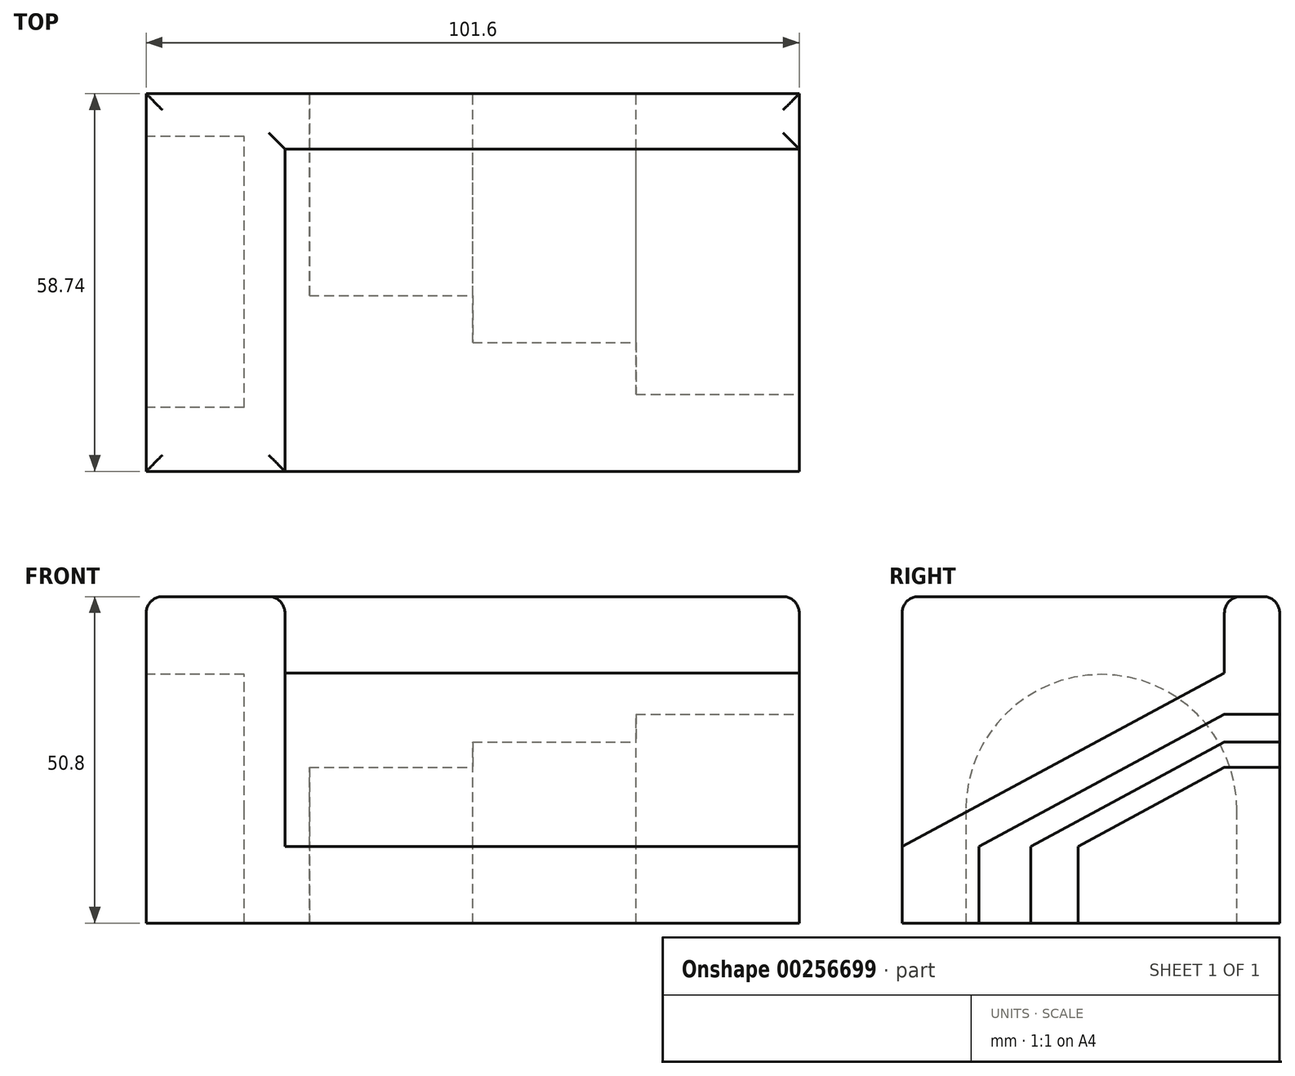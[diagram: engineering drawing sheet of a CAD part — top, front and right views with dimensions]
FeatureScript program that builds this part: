
annotation { "Feature Type Name" : "Feature", "Feature Type Description" : "" }
export const myFeature = defineFeature(function(context is Context, id is Id, definition is map)
    precondition{}
    {
        {
            var Q0;
            Q0=qCreatedBy(makeId("Top.planeOp"),FACE);
            var sketch = newSketch(context, id + "F0", { "sketchPlane" : qUnion([Q0])});
            skLineSegment(sketch, "E0.bottom", {"start": v(38.1, 29.37) * mm, "end": v(-38.1, 29.37) * mm});
            skLineSegment(sketch, "E0.top", {"start": v(38.1, -29.37) * mm, "end": v(-38.1, -29.37) * mm});
            skLineSegment(sketch, "E0.left", {"start": v(38.1, 29.37) * mm, "end": v(38.1, -29.37) * mm});
            skLineSegment(sketch, "E0.right", {"start": v(-38.1, 29.37) * mm, "end": v(-38.1, -29.37) * mm});
            skPoint(sketch, "E0.middle", {"position": v(0, 0) * mm});
            skLineSegment(sketch, "E1.bottom", {"start": v(-38.1, -29.37) * mm, "end": v(-50.8, -29.37) * mm});
            skLineSegment(sketch, "E1.top", {"start": v(-38.1, 29.37) * mm, "end": v(-50.8, 29.37) * mm});
            skLineSegment(sketch, "E1.left", {"start": v(-38.1, -29.37) * mm, "end": v(-38.1, 29.37) * mm});
            skLineSegment(sketch, "E1.right", {"start": v(-50.8, -29.37) * mm, "end": v(-50.8, 29.37) * mm});
            skLineSegment(sketch, "E2.bottom", {"start": v(38.1, 29.37) * mm, "end": v(50.8, 29.37) * mm});
            skLineSegment(sketch, "E2.top", {"start": v(38.1, -29.37) * mm, "end": v(50.8, -29.37) * mm});
            skLineSegment(sketch, "E2.right", {"start": v(50.8, 29.37) * mm, "end": v(50.8, -29.37) * mm});
            skSolve(sketch);
        }
        {
            var Q0;
            Q0 = qSketchRegion(id + "F0", true);
            extrude(context, id + "F1", {"entities" : qUnion([Q0]), "depth" : 50.8 * mm});
        }
        {
            var Q0;
            Q0=makeQuery(id+"F1.opExtrude","SWEPT_FACE",FACE,{"disambiguationData":[OSD([sQuery(id+"F0.wireOp",EDGE,"E1.right")])]});
            var sketch = newSketch(context, id + "F2", { "sketchPlane" : qUnion([Q0])});
            skLineSegment(sketch, "E3", {"start": v(-22.71, 0) * mm, "end": v(-22.71, 17.6) * mm});
            skLineSegment(sketch, "E4", {"start": v(19.45, 17.6) * mm, "end": v(19.45, 0) * mm});
            skArc(sketch, "E5", {"start": v(19.45, 17.6) * mm, "mid": v(-1.63, 38.68) * mm, "end": v(-22.71, 17.6) * mm});
            skSolve(sketch);
        }
        {
            var Q0;
            {var subQ0=sQuery(id+"F2.wireOp",EDGE,"E3");Q0=makeQuery(id+"F2.imprint","IMPRINT",FACE,{"disambiguationData":[TD([[makeQuery(id+"F2.imprint","IMPRINT",EDGE,{"derivedFrom":subQ0}),-1.0]])]});}
            extrude(context, id + "F3", {"entities" : qUnion([Q0]), "operationType" : NewBodyOperationType.REMOVE, "oppositeDirection" : true, "depth" : 15.24 * mm});
        }
        {
            var Q0;
            Q0=makeQuery(id+"F1.opExtrude","SWEPT_FACE",FACE,{"disambiguationData":[OSD([sQuery(id+"F0.wireOp",EDGE,"E2.right")])]});
            var sketch = newSketch(context, id + "F4", { "sketchPlane" : qUnion([Q0])});
            skLineSegment(sketch, "E6", {"start": v(-29.37, 11.94) * mm, "end": v(20.78, 38.92) * mm});
            skLineSegment(sketch, "E7", {"start": v(20.78, 38.92) * mm, "end": v(20.78, 50.8) * mm});
            skLineSegment(sketch, "E8", {"start": v(20.78, 50.8) * mm, "end": v(-29.37, 50.8) * mm});
            skLineSegment(sketch, "E9", {"start": v(-29.37, 50.8) * mm, "end": v(-29.37, 11.94) * mm});
            skSolve(sketch);
        }
        {
            var Q0;
            Q0 = qSketchRegion(id + "F4", true);
            extrude(context, id + "F5", {"entities" : qUnion([Q0]), "operationType" : NewBodyOperationType.REMOVE, "oppositeDirection" : true, "depth" : 80 * mm});
        }
        {
            var Q0;
            Q0=makeQuery(id+"F1.opExtrude","SWEPT_FACE",FACE,{"disambiguationData":[OSD([sQuery(id+"F0.wireOp",EDGE,"E2.right")])]});
            var sketch = newSketch(context, id + "F6", { "sketchPlane" : qUnion([Q0])});
            skLineSegment(sketch, "E10", {"start": v(-17.42, 0) * mm, "end": v(-17.42, 11.94) * mm});
            skLineSegment(sketch, "E11", {"start": v(-17.42, 11.94) * mm, "end": v(20.78, 32.49) * mm});
            skLineSegment(sketch, "E12", {"start": v(20.78, 0) * mm, "end": v(-17.42, 0) * mm});
            skLineSegment(sketch, "E13", {"start": v(20.78, 32.49) * mm, "end": v(29.37, 32.49) * mm});
            skLineSegment(sketch, "E14", {"start": v(29.37, 32.49) * mm, "end": v(29.37, 0) * mm});
            skLineSegment(sketch, "E15", {"start": v(29.37, 0) * mm, "end": v(20.78, 0) * mm});
            skSolve(sketch);
        }
        {
            var Q0;
            Q0 = qSketchRegion(id + "F6", true);
            extrude(context, id + "F7", {"entities" : qUnion([Q0]), "operationType" : NewBodyOperationType.REMOVE, "oppositeDirection" : true, "depth" : 25.4 * mm});
        }
        {
            var Q0;
            Q0=makeQuery(id+"F1.opExtrude","CAP_FACE",FACE,{"disambiguationData":[OSD([sQuery(id+"F0.wireOp",EDGE,"E0.bottom"),sQuery(id+"F0.wireOp",EDGE,"E0.top"),sQuery(id+"F0.wireOp",EDGE,"E1.bottom"),sQuery(id+"F0.wireOp",EDGE,"E1.top"),sQuery(id+"F0.wireOp",EDGE,"E1.right"),sQuery(id+"F0.wireOp",EDGE,"E2.bottom"),sQuery(id+"F0.wireOp",EDGE,"E2.top"),sQuery(id+"F0.wireOp",EDGE,"E2.right")])],"isStart":false});
            var Q1;
            Q1=makeQuery(id+"F3.boolean.opBoolean","COPY",EDGE,{"derivedFrom":makeQuery(id+"F3.opExtrude","CAP_EDGE",EDGE,{"disambiguationData":[OSD([sQuery(id+"F2.wireOp",EDGE,"E5")])],"isStart":true})});
            fillet(context, id + "F8", {"entities" : qUnion([Q0, Q1]), "radius" : 2.54 * mm, "tangentPropagation" : true, "allowEdgeOverflow" : false});
        }
        {
            var Q0;
            Q0=makeQuery(id+"F7.boolean.opBoolean","COPY",FACE,{"derivedFrom":makeQuery(id+"F7.opExtrude","CAP_FACE",FACE,{"disambiguationData":[OSD([sQuery(id+"F6.wireOp",EDGE,"E10"),sQuery(id+"F6.wireOp",EDGE,"E11"),sQuery(id+"F6.wireOp",EDGE,"E12"),sQuery(id+"F6.wireOp",EDGE,"E13"),sQuery(id+"F6.wireOp",EDGE,"E14"),sQuery(id+"F6.wireOp",EDGE,"E15")])],"isStart":false})});
            var sketch = newSketch(context, id + "F9", { "sketchPlane" : qUnion([Q0])});
            skLineSegment(sketch, "E16", {"start": v(-9.33, 0) * mm, "end": v(-9.33, 11.94) * mm});
            skLineSegment(sketch, "E17", {"start": v(-9.33, 11.94) * mm, "end": v(20.78, 28.14) * mm});
            skLineSegment(sketch, "E18", {"start": v(20.78, 28.14) * mm, "end": v(29.37, 28.14) * mm});
            skLineSegment(sketch, "E19", {"start": v(29.37, 28.14) * mm, "end": v(29.37, 0) * mm});
            skLineSegment(sketch, "E20", {"start": v(29.37, 0) * mm, "end": v(-9.33, 0) * mm});
            skSolve(sketch);
        }
        {
            var Q0;
            Q0 = qSketchRegion(id + "F9", true);
            extrude(context, id + "F10", {"entities" : qUnion([Q0]), "operationType" : NewBodyOperationType.REMOVE, "oppositeDirection" : true, "depth" : 25.4 * mm});
        }
        {
            var Q0;
            Q0=qCreatedBy(makeId("Top.planeOp"),FACE);
            var sketch = newSketch(context, id + "F11", { "sketchPlane" : qUnion([Q0])});
            skLineSegment(sketch, "E21.bottom", {"start": v(67.07, 3) * mm, "end": v(23.4, 3) * mm});
            skLineSegment(sketch, "E21.top", {"start": v(67.07, 30.2) * mm, "end": v(23.4, 30.2) * mm});
            skLineSegment(sketch, "E21.left", {"start": v(67.07, 3) * mm, "end": v(67.07, 30.2) * mm});
            skLineSegment(sketch, "E21.right", {"start": v(23.4, 3) * mm, "end": v(23.4, 30.2) * mm});
            skSolve(sketch);
        }
        {
            var Q0;
            Q0 = qSketchRegion(id + "F11", true);
            extrude(context, id + "F12", {"entities" : qUnion([Q0]), "operationType" : NewBodyOperationType.REMOVE, "oppositeDirection" : true, "depth" : 25.4 * mm});
        }
        {
            var Q0;
            Q0=makeQuery(id+"F10.boolean.opBoolean","COPY",FACE,{"derivedFrom":makeQuery(id+"F10.opExtrude","CAP_FACE",FACE,{"disambiguationData":[OSD([sQuery(id+"F9.wireOp",EDGE,"E16"),sQuery(id+"F9.wireOp",EDGE,"E17"),sQuery(id+"F9.wireOp",EDGE,"E18"),sQuery(id+"F9.wireOp",EDGE,"E19"),sQuery(id+"F9.wireOp",EDGE,"E20")])],"isStart":false})});
            var sketch = newSketch(context, id + "F13", { "sketchPlane" : qUnion([Q0])});
            skLineSegment(sketch, "E22", {"start": v(-2.01, 0) * mm, "end": v(-2.01, 11.94) * mm});
            skLineSegment(sketch, "E23", {"start": v(-2.01, 11.94) * mm, "end": v(20.78, 24.2) * mm});
            skLineSegment(sketch, "E24", {"start": v(20.78, 24.2) * mm, "end": v(29.37, 24.2) * mm});
            skLineSegment(sketch, "E25", {"start": v(29.37, 24.2) * mm, "end": v(29.37, 0) * mm});
            skLineSegment(sketch, "E26", {"start": v(29.37, 0) * mm, "end": v(-2.01, 0) * mm});
            skSolve(sketch);
        }
        {
            var Q0;
            Q0 = qSketchRegion(id + "F13", true);
            extrude(context, id + "F14", {"entities" : qUnion([Q0]), "operationType" : NewBodyOperationType.REMOVE, "oppositeDirection" : true, "depth" : 25.4 * mm});
        }
    });
